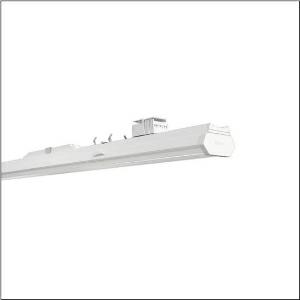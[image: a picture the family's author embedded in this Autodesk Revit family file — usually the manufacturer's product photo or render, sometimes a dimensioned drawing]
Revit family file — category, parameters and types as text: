
# Revit family: licross_r__21_protected_ho_52td12dn4e5m3s4_bb7a
name_source: partatom
category: Lighting Fixtures
units: mm (PartAtom-declared; Revit-internal decimal feet)

## family parameters
Cut with Voids When Loaded = No
Host = Face
Light Source = No
Part Type = Normal
Room Calculation Point = No
Round Connector Dimension = Use Diameter
Shared = No

## types (1)
- --- (1 x LED, 910 lm, 7.6 W, 4000K)
    Apparent Load = 8 VA
    CIE Flux Codes = 70 91 97 98 100
    Color Rendering = 80
    Color Temperature = 4000K
    Default Elevation = 1800 mm
    Description = Licross® 21 Protected HO, luminaire insert, of sheet steel, galvanised, coil coated, white, length: 1.500mm, width: 90mm, height: 103mm, LED rated luminous flux: 14.690lm, light colour: 840, control gear: DALI 2, with plug, 6-pole, with phase selection, for trunking rail, 9 or 11-core, mains connection: 220..240V, AC, 50/60Hz, rated input power: 89W, for trunking rail, 9-/11-core, halogen-free wiring, for emergency light function, converter,control gear: single battery element, battery: LiFePO4, 9Ah, primary light control with lens, of plastic, primary optical cover: cover, of PMMA, light emission: direct distribution, primary light characteristic: symmetric, protection rating (complete): IP54, insulation class (complete): insulation class I (protective earthing), certification: CE, UKCA, protection symbol: D if used in an environment with non-conductive dust loads with corresponding accessories, impact resistance: IK06, permissible ambient temperature for indoor applications: +5..+30°C, standard: EN 60598-2-22, LABS conformity tested according to VDMA 24364:2018-05, reducing of maximum allowable ambient temperature of 5°C with ceiling mounting, corresponds to IFS (International Featured Standards) requirements for safety and quality in the food industry, packaging unit: 1 piece
    Height = 92 mm
    Lamp = 1 x LED
    Lamp Light Flux = 910 lm
    Lamp Power = 7.6 W
    Lamp count = 1
    Length = 1500 mm
    Luminous efficacy = 120 lm/W
    Manufacturer = Siteco
    ModVariant = No
    Model = 52TD12DN4E5M3S4
    Mounting Place = Ceiling
    Mounting Type = Pendant
    Number of Poles = 1
    OnlyDefault = Yes
    Power Factor = 1
    Product Name = Licross® 21 Protected HO
    Product group = luminaire insert
    ProductGroupID = 902
    Protection Class = Protection class I
    Protection Degree = IP 54
    RLX_Detail_Level = 1
    RLX_Emergency_Light_Flux = 0 lm
    RLX_Emergency_Type = 0
    RLX_Emergency_Type_DB = No
    RlxData = <blob elided: 24825 chars, md5=ae4cf5f6>
    Socket = socket
    Standby Power = 0 W
    System Light Flux = 910 lm
    System Power = 8 W
    Type Comments = : emergency light operation: 3 h
    Type Image = l_1256148.jpg
    URL = http://relux.com
    VarID = @adj_111224
    Voltage = 0 V
    Weight = 0.00 kg
    Width = 88 mm

## geometry (parser evidence)
native form markers: Blend x4, Sweep x10
no freeform markers — native parametric forms only
